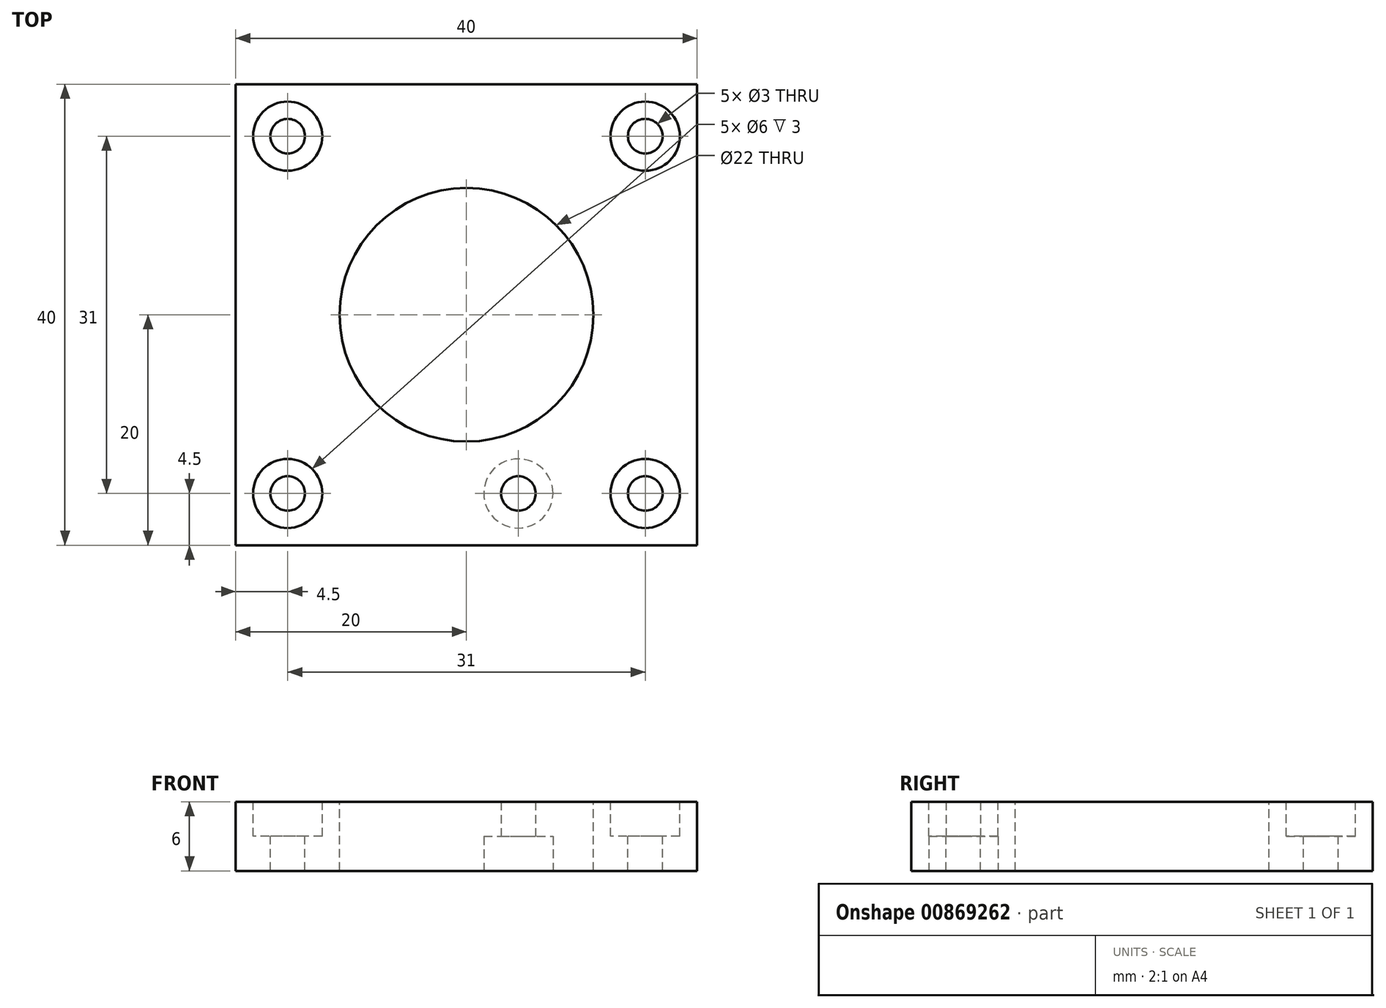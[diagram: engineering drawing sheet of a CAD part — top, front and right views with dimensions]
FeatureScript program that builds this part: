
annotation { "Feature Type Name" : "Feature", "Feature Type Description" : "" }
export const myFeature = defineFeature(function(context is Context, id is Id, definition is map)
    precondition{}
    {
        {
            var Q0;
            Q0=qCreatedBy(makeId("Top.planeOp"),FACE);
            var sketch = newSketch(context, id + "F0", { "sketchPlane" : qUnion([Q0])});
            skLineSegment(sketch, "E0.bottom", {"start": v(20, -20) * mm, "end": v(-20, -20) * mm});
            skLineSegment(sketch, "E0.top", {"start": v(20, 20) * mm, "end": v(-20, 20) * mm});
            skLineSegment(sketch, "E0.left", {"start": v(20, -20) * mm, "end": v(20, 20) * mm});
            skLineSegment(sketch, "E0.right", {"start": v(-20, -20) * mm, "end": v(-20, 20) * mm});
            skPoint(sketch, "E0.middle", {"position": v(0, 0) * mm});
            skLineSegment(sketch, "E1", {"start": v(0, -20) * mm, "end": v(0, -14) * mm});
            skLineSegment(sketch, "E2", {"start": v(0, -14) * mm, "end": v(15, -14) * mm});
            skLineSegment(sketch, "E3", {"start": v(0, -20) * mm, "end": v(0, -15.5) * mm});
            skLineSegment(sketch, "E4", {"start": v(0, -15.5) * mm, "end": v(15.5, -15.5) * mm});
            skLineSegment(sketch, "E5", {"start": v(0, -15.5) * mm, "end": v(-15.5, -15.5) * mm});
            skLineSegment(sketch, "E6.bottom", {"start": v(15.5, -15.5) * mm, "end": v(-15.5, -15.5) * mm});
            skLineSegment(sketch, "E6.top", {"start": v(15.5, 15.5) * mm, "end": v(-15.5, 15.5) * mm});
            skLineSegment(sketch, "E6.left", {"start": v(15.5, -15.5) * mm, "end": v(15.5, 15.5) * mm});
            skLineSegment(sketch, "E6.right", {"start": v(-15.5, -15.5) * mm, "end": v(-15.5, 15.5) * mm});
            skCircle(sketch, "E7", {"center": v(0, 0) * mm, "radius": 11 * mm});
            skLineSegment(sketch, "E8", {"start": v(0, -14) * mm, "end": v(5, -14) * mm});
            skPoint(sketch, "E9", {"position": v(5, -14) * mm});
            skSolve(sketch);
        }
        {
            var Q0;
            Q0=makeQuery(id+"F0.imprint","IMPRINT",FACE,{"disambiguationData":[TD([[makeQuery(id+"F0.imprint","IMPRINT",EDGE,{"derivedFrom":sQuery(id+"F0.wireOp",EDGE,"E6.top")}),1.0]])]});
            var Q1;
            Q1=makeQuery(id+"F0.imprint","IMPRINT",FACE,{"disambiguationData":[TD([[makeQuery(id+"F0.imprint","IMPRINT",EDGE,{"derivedFrom":sQuery(id+"F0.wireOp",EDGE,"E0.top")}),1.0]])]});
            var Q2;
            {var subQ1=sQuery(id+"F0.wireOp",EDGE,"E1");Q2=makeQuery(id+"F0.imprint","IMPRINT",FACE,{"disambiguationData":[TD([[makeQuery(id+"F0.imprint","IMPRINT",EDGE,{"derivedFrom":subQ1}),-1.0]])]});}
            extrude(context, id + "F1", {"entities" : qUnion([Q0, Q1, Q2]), "surfaceOperationType" : NewSurfaceOperationType.ADD, "oppositeDirection" : true, "depth" : 6 * mm, "offsetDistance" : 25 * mm});
        }
        {
            var Q0;
            Q0=sQuery(id+"F0.wireOp",VERTEX,"E6.top.start");
            var Q1;
            Q1=sQuery(id+"F0.wireOp",VERTEX,"E4.end");
            var Q2;
            Q2=sQuery(id+"F0.wireOp",VERTEX,"E5.end");
            var Q3;
            Q3=sQuery(id+"F0.wireOp",VERTEX,"E6.top.end");
            var Q4;
            Q4=makeQuery(id+"F1.opExtrude","SWEPT_BODY",BODY,{"disambiguationData":[OSD([sQuery(id+"F0.wireOp",EDGE,"E0.bottom"),sQuery(id+"F0.wireOp",EDGE,"E0.top"),sQuery(id+"F0.wireOp",EDGE,"E0.left"),sQuery(id+"F0.wireOp",EDGE,"E0.right"),sQuery(id+"F0.wireOp",EDGE,"E7")])]});
            hole(context, id + "F2", {"style" : HoleStyle.C_BORE, "endStyle" : HoleEndStyle.THROUGH, "holeDiameter" : 3 * mm, "cBoreDiameter" : 6 * mm, "cBoreDepth" : 3 * mm, "majorDiameter" : 5 * mm, "isTappedThrough" : true, "tappedDepth" : 12 * mm, "tapClearance" : 3, "locations" : qUnion([Q0, Q1, Q2, Q3]), "scope" : qUnion([Q4])});
        }
        {
            var Q0;
            Q0=makeQuery(id+"F1.opExtrude","CAP_FACE",FACE,{"disambiguationData":[OSD([sQuery(id+"F0.wireOp",EDGE,"E0.bottom"),sQuery(id+"F0.wireOp",EDGE,"E0.top"),sQuery(id+"F0.wireOp",EDGE,"E0.left"),sQuery(id+"F0.wireOp",EDGE,"E0.right"),sQuery(id+"F0.wireOp",EDGE,"E7")])],"isStart":false});
            var sketch = newSketch(context, id + "F3", { "sketchPlane" : qUnion([Q0])});
            skLineSegment(sketch, "E10", {"start": v(0, 20) * mm, "end": v(0, 14) * mm});
            skLineSegment(sketch, "E11", {"start": v(0, 14) * mm, "end": v(7.5, 14) * mm});
            skLineSegment(sketch, "E12", {"start": v(7.5, 14) * mm, "end": v(4.5, 14) * mm});
            skLineSegment(sketch, "E13", {"start": v(7.5, 14) * mm, "end": v(10.5, 14) * mm});
            skLineSegment(sketch, "E14", {"start": v(4.5, 14) * mm, "end": v(4.5, 15.5) * mm});
            skLineSegment(sketch, "E15", {"start": v(10.5, 14) * mm, "end": v(10.5, 12) * mm});
            skSolve(sketch);
        }
        {
            var Q0;
            Q0=sQuery(id+"F3.wireOp",VERTEX,"E14.end");
            var Q1;
            Q1=makeQuery(id+"F1.opExtrude","SWEPT_BODY",BODY,{"disambiguationData":[OSD([sQuery(id+"F0.wireOp",EDGE,"E0.bottom"),sQuery(id+"F0.wireOp",EDGE,"E0.top"),sQuery(id+"F0.wireOp",EDGE,"E0.left"),sQuery(id+"F0.wireOp",EDGE,"E0.right"),sQuery(id+"F0.wireOp",EDGE,"E7")])]});
            hole(context, id + "F4", {"style" : HoleStyle.C_BORE, "endStyle" : HoleEndStyle.THROUGH, "holeDiameter" : 3 * mm, "cBoreDiameter" : 6 * mm, "cBoreDepth" : 3 * mm, "majorDiameter" : 5 * mm, "isTappedThrough" : true, "tappedDepth" : 12 * mm, "tapClearance" : 3, "locations" : qUnion([Q0]), "scope" : qUnion([Q1])});
        }
    });
